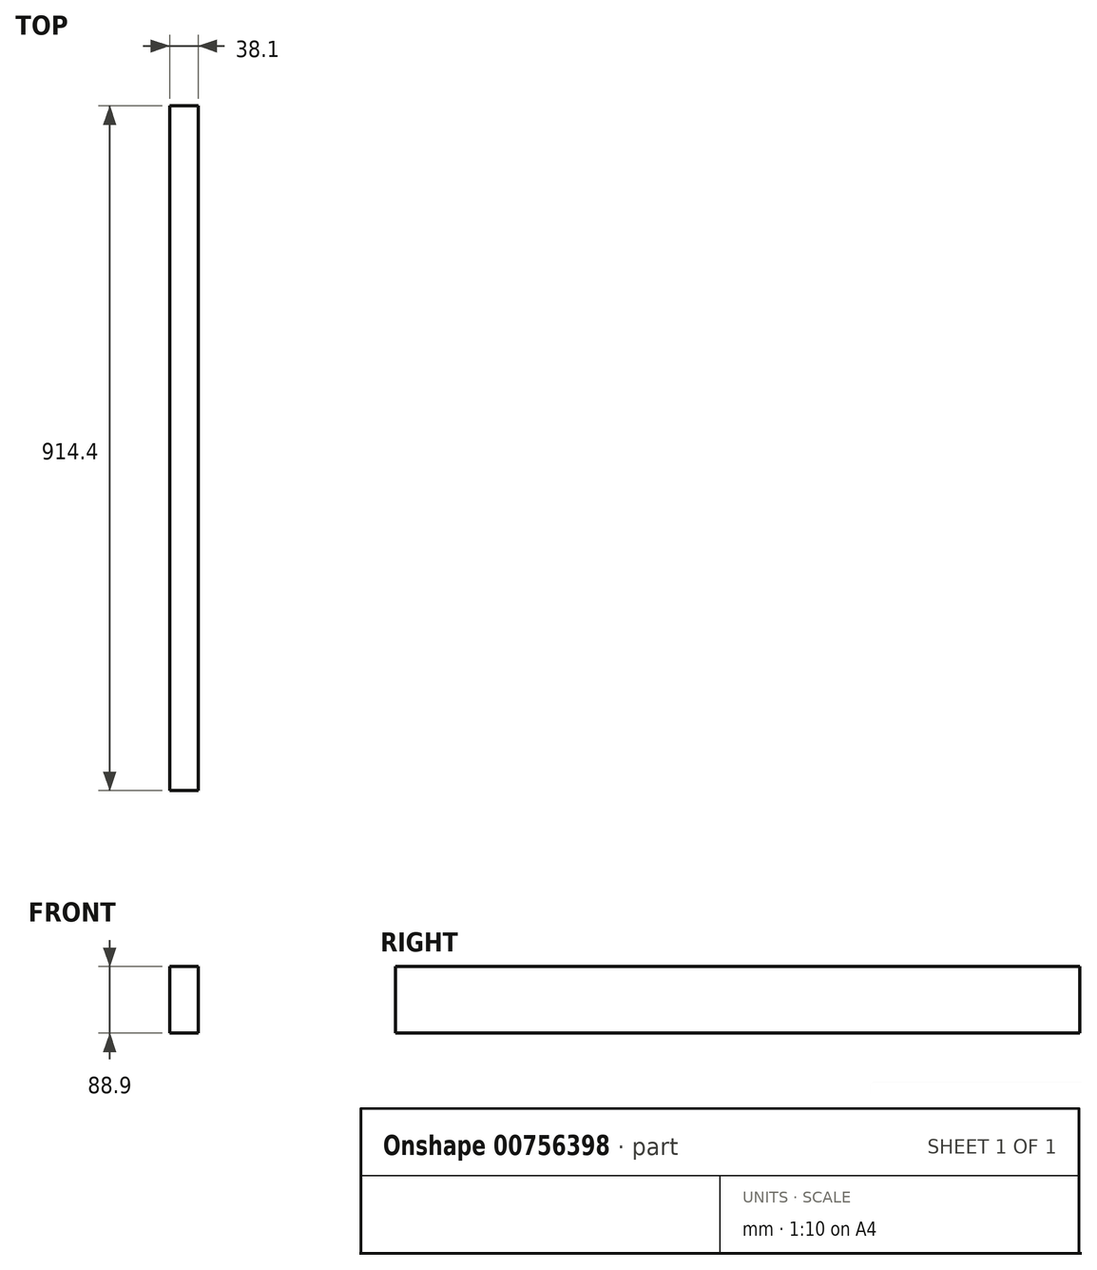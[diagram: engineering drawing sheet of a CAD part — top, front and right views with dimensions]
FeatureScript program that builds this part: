
annotation { "Feature Type Name" : "Feature", "Feature Type Description" : "" }
export const myFeature = defineFeature(function(context is Context, id is Id, definition is map)
    precondition{}
    {
        {
            var Q0;
            Q0=qCreatedBy(makeId("Front.planeOp"),FACE);
            var sketch = newSketch(context, id + "F0", { "sketchPlane" : qUnion([Q0])});
            skLineSegment(sketch, "E0.bottom", {"start": v(0, 88.9) * mm, "end": v(38.1, 88.9) * mm});
            skLineSegment(sketch, "E0.top", {"start": v(0, 0) * mm, "end": v(38.1, 0) * mm});
            skLineSegment(sketch, "E0.left", {"start": v(0, 88.9) * mm, "end": v(0, 0) * mm});
            skLineSegment(sketch, "E0.right", {"start": v(38.1, 88.9) * mm, "end": v(38.1, 0) * mm});
            skPoint(sketch, "E1.visualSharp", {"position": v(0, 88.9) * mm});
            skPoint(sketch, "E2.visualSharp", {"position": v(38.1, 88.9) * mm});
            skPoint(sketch, "E3.visualSharp", {"position": v(0, 0) * mm});
            skPoint(sketch, "E4.visualSharp", {"position": v(38.1, 0) * mm});
            skSolve(sketch);
        }
        {
            var Q0;
            Q0=makeQuery(id+"F0.imprint","IMPRINT",FACE,{"disambiguationData":[TD([[makeQuery(id+"F0.imprint","IMPRINT",EDGE,{"derivedFrom":sQuery(id+"F0.wireOp",EDGE,"E0.bottom")}),-1.0]])]});
            extrude(context, id + "F1", {"entities" : qUnion([Q0]), "depth" : 914.4 * mm, "offsetDistance" : 25.4 * mm});
        }
    });
